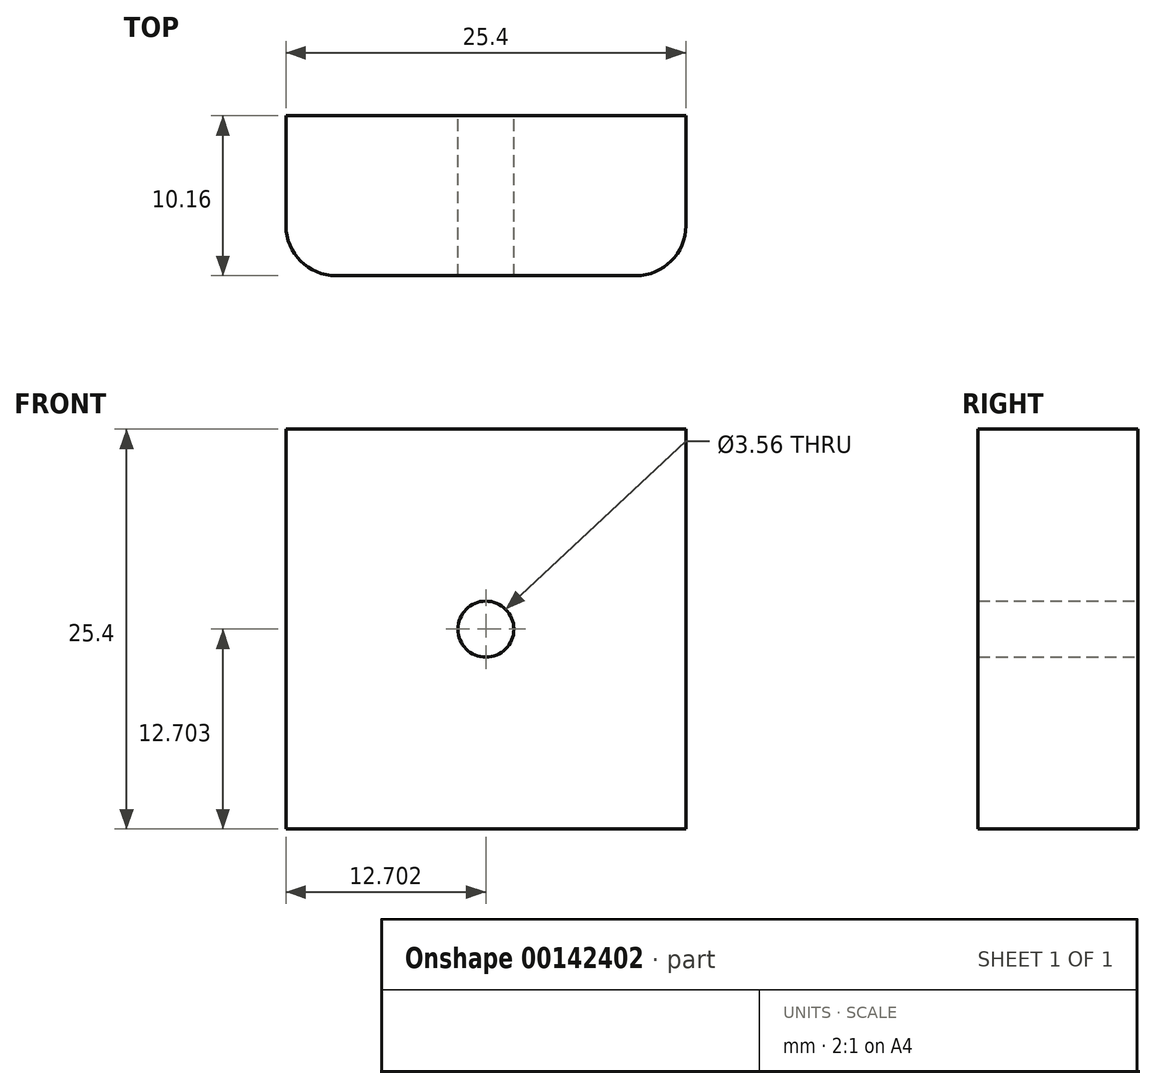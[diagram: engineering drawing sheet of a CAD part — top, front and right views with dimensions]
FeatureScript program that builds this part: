
annotation { "Feature Type Name" : "Feature", "Feature Type Description" : "" }
export const myFeature = defineFeature(function(context is Context, id is Id, definition is map)
    precondition{}
    {
        {
            var Q0;
            Q0=qCreatedBy(makeId("Front.planeOp"),FACE);
            var sketch = newSketch(context, id + "F0", { "sketchPlane" : qUnion([Q0])});
            skLineSegment(sketch, "E0.bottom", {"start": v(6.26, 2.15) * mm, "end": v(31.66, 2.15) * mm});
            skLineSegment(sketch, "E0.top", {"start": v(6.26, -23.25) * mm, "end": v(31.66, -23.25) * mm});
            skLineSegment(sketch, "E0.left", {"start": v(6.26, 2.15) * mm, "end": v(6.26, -23.25) * mm});
            skLineSegment(sketch, "E0.right", {"start": v(31.66, 2.15) * mm, "end": v(31.66, -23.25) * mm});
            skCircle(sketch, "E1", {"center": v(18.96, -10.55) * mm, "radius": 1.78 * mm});
            skSolve(sketch);
        }
        {
            var Q0;
            Q0=makeQuery(id+"F0.imprint","IMPRINT",FACE,{"disambiguationData":[TD([[makeQuery(id+"F0.imprint","IMPRINT",EDGE,{"derivedFrom":sQuery(id+"F0.wireOp",EDGE,"E0.bottom")}),-1.0]])]});
            extrude(context, id + "F1", {"entities" : qUnion([Q0]), "depth" : 10.16 * mm});
        }
        {
            var Q0;
            Q0=makeQuery(id+"F1.opExtrude","CAP_EDGE",EDGE,{"disambiguationData":[OSD([sQuery(id+"F0.wireOp",EDGE,"E0.left")])],"isStart":false});
            var Q1;
            Q1=makeQuery(id+"F1.opExtrude","CAP_EDGE",EDGE,{"disambiguationData":[OSD([sQuery(id+"F0.wireOp",EDGE,"E0.right")])],"isStart":false});
            fillet(context, id + "F2", {"entities" : qUnion([Q0, Q1]), "radius" : 3.17 * mm, "tangentPropagation" : true, "allowEdgeOverflow" : false});
        }
    });
